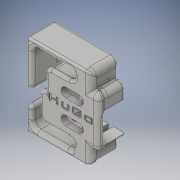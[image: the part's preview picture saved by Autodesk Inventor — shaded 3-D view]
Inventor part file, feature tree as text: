
AUTODESK INVENTOR PART (.ipt)
format: ipt  version: 2016 (Build 200138000, 138)  size: 858,112 bytes
history: native  units: in
note: dims shown in document units (in); Inventor stores cm internally (conversion verified against a paired STEP export)
features: sketch x21, other x3, plane x2
ambient origin geometry x8: Origin, YZ Plane, XZ Plane, XY Plane, X Axis, Y Axis, Z Axis, Center Point
bodies: Solid1 (feature_tree)
feature tree (26):
  other  "Hip_rotation_temp_MIR.ipt"
  other  "Solid1::Hip_rotation_temp_MIR.ipt"
  other  "TaggingFeature1"
  sketch  "Sketch1"  dims[d0=0.3937in]
  sketch  "Sketch12"
  sketch  "Sketch14"
  sketch  "Sketch17"
  sketch  "Sketch18"
  sketch  "Sketch20"
  sketch  "Sketch21"
  sketch  "Sketch22"
  sketch  "Sketch25"
  sketch  "Sketch26"
  sketch  "Sketch27"
  sketch  "Sketch13"
  sketch  "Sketch15"
  sketch  "Sketch16"
  sketch  "Sketch24"
  sketch  "Sketch28"
  sketch  "Sketch29"
  sketch  "Sketch31"
  sketch  "Sketch32"
  sketch  "Sketch34"
  sketch  "Sketch35"
  plane  "Work Plane1"
  plane  "Work Plane2"
